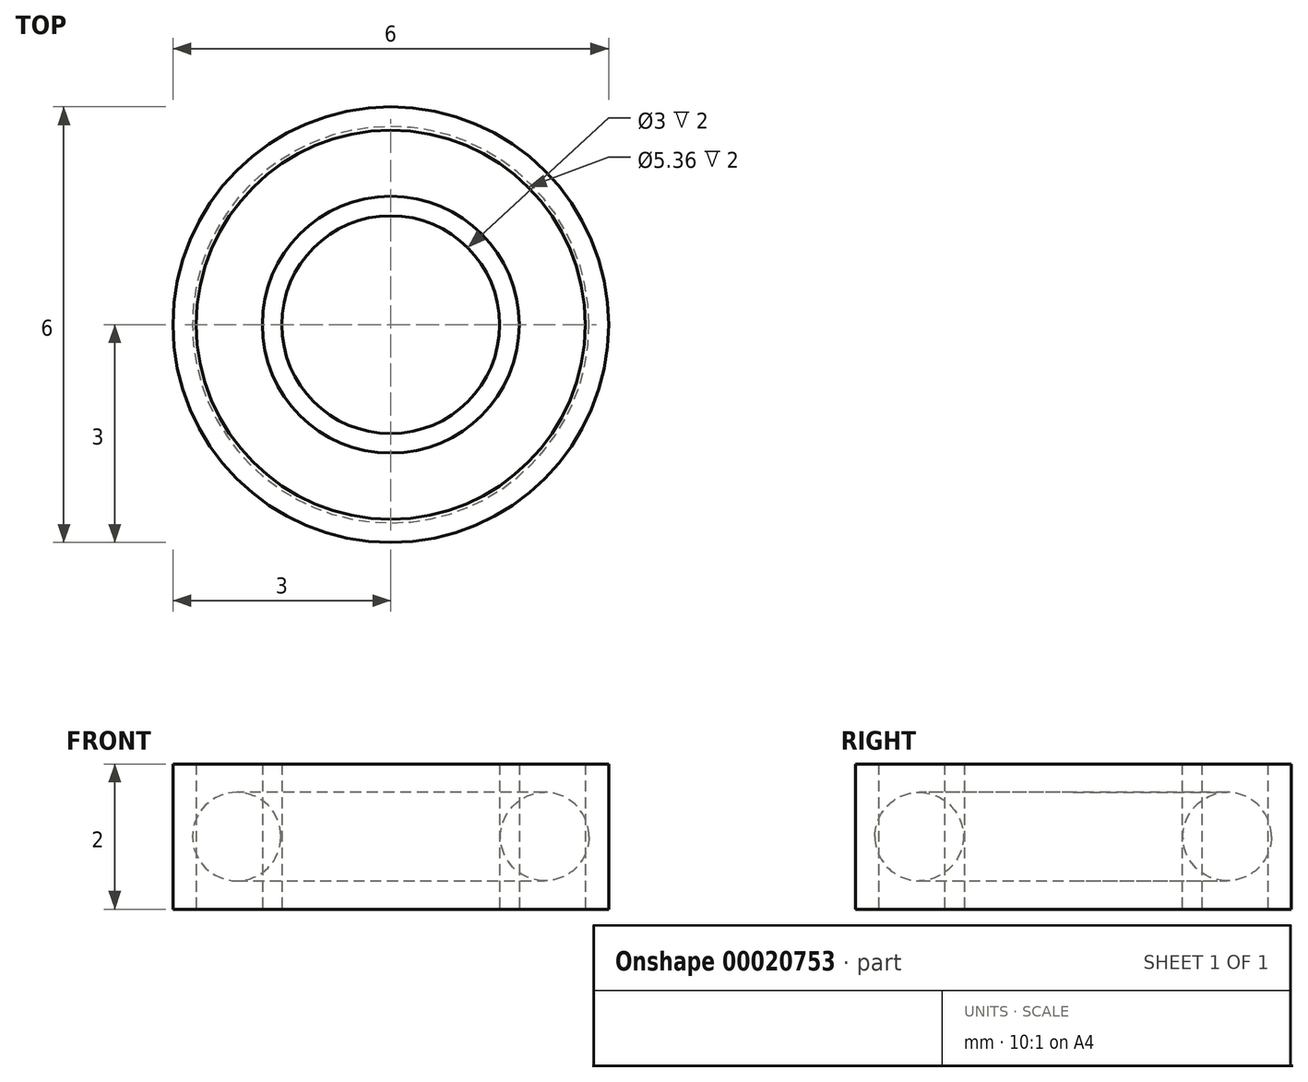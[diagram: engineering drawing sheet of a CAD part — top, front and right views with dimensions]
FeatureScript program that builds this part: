
annotation { "Feature Type Name" : "Feature", "Feature Type Description" : "" }
export const myFeature = defineFeature(function(context is Context, id is Id, definition is map)
    precondition{}
    {
        {
            var Q0;
            Q0=qCreatedBy(makeId("Top.planeOp"),FACE);
            var sketch = newSketch(context, id + "F0", { "sketchPlane" : qUnion([Q0])});
            skCircle(sketch, "E0", {"center": v(0, 0) * mm, "radius": 3 * mm});
            skCircle(sketch, "E1", {"center": v(0, 0) * mm, "radius": 1.5 * mm});
            skCircle(sketch, "E2", {"center": v(0, 0) * mm, "radius": 1.77 * mm});
            skCircle(sketch, "E3", {"center": v(0, 0) * mm, "radius": 2.68 * mm});
            skCircle(sketch, "E4", {"center": v(0, 0) * mm, "radius": 2.19 * mm});
            skSolve(sketch);
        }
        {
            var Q0;
            Q0=makeQuery(id+"F0.imprint","IMPRINT",FACE,{"disambiguationData":[TD([[makeQuery(id+"F0.imprint","IMPRINT",EDGE,{"derivedFrom":sQuery(id+"F0.wireOp",EDGE,"E0")}),1.0]])]});
            extrude(context, id + "F1", {"entities" : qUnion([Q0]), "depth" : 2 * mm});
        }
        {
            var Q0;
            Q0=makeQuery(id+"F0.imprint","IMPRINT",FACE,{"disambiguationData":[TD([[makeQuery(id+"F0.imprint","IMPRINT",EDGE,{"derivedFrom":sQuery(id+"F0.wireOp",EDGE,"E1")}),-1.0]])]});
            extrude(context, id + "F2", {"entities" : qUnion([Q0]), "depth" : 2 * mm});
        }
        {
            var Q0;
            Q0=qCreatedBy(makeId("Front.planeOp"),FACE);
            var sketch = newSketch(context, id + "F3", { "sketchPlane" : qUnion([Q0])});
            skCircle(sketch, "E5", {"center": v(2.12, 1) * mm, "radius": 0.6 * mm});
            skSolve(sketch);
        }
        {
            var Q0;
            Q0=makeQuery(id+"F3.imprint","IMPRINT",FACE,{"disambiguationData":[TD([[makeQuery(id+"F3.imprint","IMPRINT",EDGE,{"derivedFrom":sQuery(id+"F3.wireOp",EDGE,"E5")}),1.0]])]});
            var Q1;
            Q1=sQuery(id+"F0.wireOp",EDGE,"E4");
            revolve(context, id + "F4", {"entities" : qUnion([Q0]), "axis" : qUnion([Q1]), "revolveType" : RevolveType.FULL});
        }
    });
